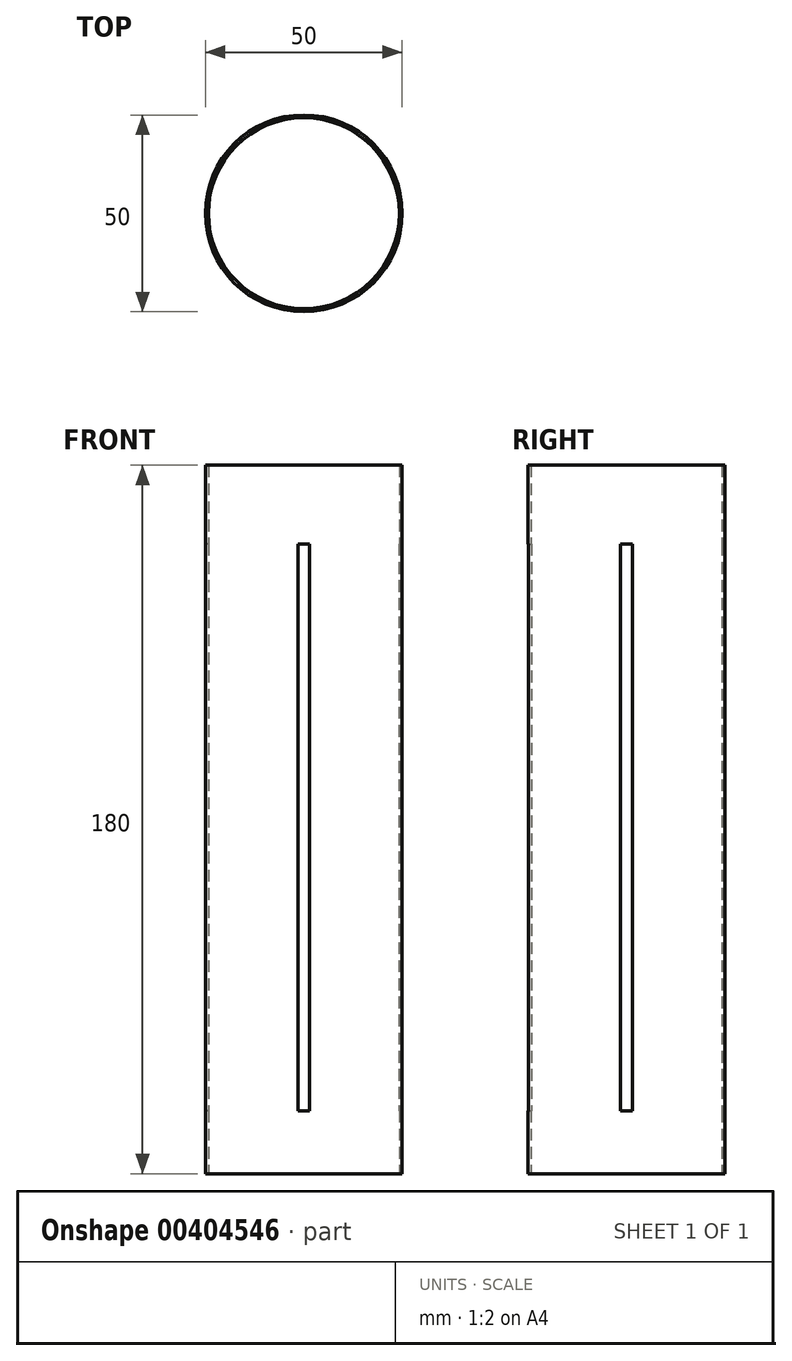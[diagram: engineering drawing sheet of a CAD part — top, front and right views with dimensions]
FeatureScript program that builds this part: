
annotation { "Feature Type Name" : "Feature", "Feature Type Description" : "" }
export const myFeature = defineFeature(function(context is Context, id is Id, definition is map)
    precondition{}
    {
        {
            var Q0;
            Q0=qCreatedBy(makeId("Top.planeOp"),FACE);
            var sketch = newSketch(context, id + "F0", { "sketchPlane" : qUnion([Q0])});
            skCircle(sketch, "E0", {"center": v(0, 0) * mm, "radius": 24.25 * mm});
            skCircle(sketch, "E1", {"center": v(0, 0) * mm, "radius": 25 * mm});
            skCircle(sketch, "E2", {"center": v(0, 0) * mm, "radius": 23.25 * mm});
            skSolve(sketch);
        }
        {
            var Q0;
            Q0=makeQuery(id+"F0.imprint","IMPRINT",FACE,{"disambiguationData":[TD([[makeQuery(id+"F0.imprint","IMPRINT",EDGE,{"derivedFrom":sQuery(id+"F0.wireOp",EDGE,"E0")}),-1.0]])]});
            var Q1;
            Q1 = qSketchRegion(id + "F2", true);
            extrude(context, id + "F1", {"entities" : qUnion([Q0, Q1]), "depth" : 180 * mm});
        }
        {
            var Q0;
            Q0=qCreatedBy(makeId("Right.planeOp"),FACE);
            var sketch = newSketch(context, id + "F2", { "sketchPlane" : qUnion([Q0])});
            skPoint(sketch, "E3", {"position": v(-24.8, 0) * mm});
            skPoint(sketch, "E4", {"position": v(-24.94, 16) * mm});
            skPoint(sketch, "E5", {"position": v(-24.94, 160) * mm});
            skPoint(sketch, "E6", {"position": v(24.93, 0) * mm});
            skPoint(sketch, "E7", {"position": v(24.93, 16) * mm});
            skPoint(sketch, "E8", {"position": v(24.93, 160) * mm});
            skLineSegment(sketch, "E9", {"start": v(-24.8, 0) * mm, "end": v(-24.94, 16) * mm});
            skLineSegment(sketch, "E10", {"start": v(-24.94, 16) * mm, "end": v(-24.94, 160) * mm});
            skLineSegment(sketch, "E11", {"start": v(24.93, 0) * mm, "end": v(24.93, 16) * mm});
            skLineSegment(sketch, "E12", {"start": v(24.93, 16) * mm, "end": v(24.93, 160) * mm});
            skPoint(sketch, "E13", {"position": v(-31.51, 160) * mm});
            skPoint(sketch, "E14", {"position": v(-31.6, 16) * mm});
            skPoint(sketch, "E15", {"position": v(-31.51, 0) * mm});
            skLineSegment(sketch, "E16", {"start": v(-31.51, 160) * mm, "end": v(-31.51, 0) * mm});
            skLineSegment(sketch, "E17", {"start": v(-31.51, 160) * mm, "end": v(-24.94, 160) * mm});
            skLineSegment(sketch, "E18", {"start": v(-31.51, 0) * mm, "end": v(-24.8, 0) * mm});
            skLineSegment(sketch, "E19", {"start": v(-31.6, 16) * mm, "end": v(-24.94, 16) * mm});
            skLineSegment(sketch, "E20", {"start": v(-56.53, 16) * mm, "end": v(47.01, 16) * mm});
            skLineSegment(sketch, "E21", {"start": v(-56.08, 0) * mm, "end": v(53.13, 0) * mm});
            skPoint(sketch, "E22", {"position": v(32.4, 160) * mm});
            skPoint(sketch, "E23", {"position": v(32.4, 16) * mm});
            skPoint(sketch, "E24", {"position": v(32.4, 0) * mm});
            skLineSegment(sketch, "E25", {"start": v(32.4, 160) * mm, "end": v(32.4, 16) * mm});
            skLineSegment(sketch, "E26", {"start": v(32.4, 0) * mm, "end": v(32.4, 16) * mm});
            skLineSegment(sketch, "E27", {"start": v(32.4, 160) * mm, "end": v(24.93, 160) * mm});
            skSolve(sketch);
        }
        {
            var Q0;
            {var subQ0=sQuery(id+"F2.wireOp",EDGE,"E10");Q0=makeQuery(id+"F2.imprint","IMPRINT",FACE,{"disambiguationData":[TD([[makeQuery(id+"F2.imprint","IMPRINT",EDGE,{"derivedFrom":subQ0}),1.0]])]});}
            var Q1;
            {var subQ0=sQuery(id+"F2.wireOp",EDGE,"E12");Q1=makeQuery(id+"F2.imprint","IMPRINT",FACE,{"disambiguationData":[TD([[makeQuery(id+"F2.imprint","IMPRINT",EDGE,{"derivedFrom":subQ0}),-1.0]])]});}
            extrude(context, id + "F3", {"entities" : qUnion([Q0, Q1]), "operationType" : NewBodyOperationType.REMOVE, "endBound" : BoundingType.SYMMETRIC, "depth" : 3 * mm});
        }
        {
            var Q0;
            Q0=makeQuery(id+"F3.boolean.opBoolean","COPY",FACE,{"derivedFrom":makeQuery(id+"F3.opExtrude","SWEPT_FACE",FACE,{"disambiguationData":[OSD([sQuery(id+"F2.wireOp",EDGE,"E10")])]})});
            var Q1;
            Q1=makeQuery(id+"F3.boolean.opBoolean","COPY",FACE,{"derivedFrom":makeQuery(id+"F3.opExtrude","SWEPT_FACE",FACE,{"disambiguationData":[OSD([sQuery(id+"F2.wireOp",EDGE,"E12")])]})});
            extrude(context, id + "F4", {"entities" : qUnion([Q0, Q1]), "operationType" : NewBodyOperationType.REMOVE, "oppositeDirection" : true, "depth" : 4 * mm});
        }
        {
            var Q0;
            Q0=makeQuery(id+"F3.boolean.opBoolean","COPY",FACE,{"derivedFrom":makeQuery(id+"F3.opExtrude","SWEPT_FACE",FACE,{"disambiguationData":[OSD([sQuery(id+"F2.wireOp",EDGE,"E12")])]})});
            extrude(context, id + "F5", {"entities" : qUnion([Q0]), "operationType" : NewBodyOperationType.REMOVE, "oppositeDirection" : true, "depth" : 4 * mm});
        }
        {
            var Q0;
            Q0=qCreatedBy(makeId("Front.planeOp"),FACE);
            var sketch = newSketch(context, id + "F6", { "sketchPlane" : qUnion([Q0])});
            skPoint(sketch, "E28", {"position": v(-24.85, 0) * mm});
            skPoint(sketch, "E29", {"position": v(-24.7, 16) * mm});
            skPoint(sketch, "E30", {"position": v(-24.7, 160) * mm});
            skPoint(sketch, "E31", {"position": v(24.76, 0) * mm});
            skPoint(sketch, "E32", {"position": v(24.76, 16) * mm});
            skPoint(sketch, "E33", {"position": v(24.76, 160) * mm});
            skLineSegment(sketch, "E34", {"start": v(-24.85, 0) * mm, "end": v(-24.7, 16) * mm});
            skLineSegment(sketch, "E35", {"start": v(-24.7, 16) * mm, "end": v(-24.7, 160) * mm});
            skLineSegment(sketch, "E36", {"start": v(24.76, 0) * mm, "end": v(24.76, 16) * mm});
            skLineSegment(sketch, "E37", {"start": v(24.76, 16) * mm, "end": v(24.76, 160) * mm});
            skPoint(sketch, "E38", {"position": v(-31.87, 160) * mm});
            skPoint(sketch, "E39", {"position": v(-31.96, 16) * mm});
            skPoint(sketch, "E40", {"position": v(-31.87, 0) * mm});
            skLineSegment(sketch, "E41", {"start": v(-31.87, 160) * mm, "end": v(-31.87, 0) * mm});
            skLineSegment(sketch, "E42", {"start": v(-31.87, 160) * mm, "end": v(-24.7, 160) * mm});
            skLineSegment(sketch, "E43", {"start": v(-56.89, 16) * mm, "end": v(46.66, 16) * mm});
            skLineSegment(sketch, "E44", {"start": v(-56.43, 0) * mm, "end": v(52.78, 0) * mm});
            skPoint(sketch, "E45", {"position": v(32.05, 160) * mm});
            skPoint(sketch, "E46", {"position": v(32.05, 16) * mm});
            skPoint(sketch, "E47", {"position": v(32.05, 0) * mm});
            skLineSegment(sketch, "E48", {"start": v(32.05, 160) * mm, "end": v(32.05, 16) * mm});
            skLineSegment(sketch, "E49", {"start": v(32.05, 160) * mm, "end": v(24.76, 160) * mm});
            skLineSegment(sketch, "E50", {"start": v(32.05, 0) * mm, "end": v(32.05, 16) * mm});
            skSolve(sketch);
        }
        {
            var Q0;
            {var subQ0=sQuery(id+"F6.wireOp",EDGE,"E37");Q0=makeQuery(id+"F6.imprint","IMPRINT",FACE,{"disambiguationData":[TD([[makeQuery(id+"F6.imprint","IMPRINT",EDGE,{"derivedFrom":subQ0}),-1.0]])]});}
            var Q1;
            {var subQ0=sQuery(id+"F6.wireOp",EDGE,"E35");Q1=makeQuery(id+"F6.imprint","IMPRINT",FACE,{"disambiguationData":[TD([[makeQuery(id+"F6.imprint","IMPRINT",EDGE,{"derivedFrom":subQ0}),1.0]])]});}
            extrude(context, id + "F7", {"entities" : qUnion([Q0, Q1]), "operationType" : NewBodyOperationType.ADD, "endBound" : BoundingType.SYMMETRIC, "depth" : 3 * mm});
        }
        {
            var Q0;
            Q0=makeQuery(id+"F7.opExtrude","SWEPT_FACE",FACE,{"disambiguationData":[OSD([sQuery(id+"F6.wireOp",EDGE,"E48")])]});
            var Q1;
            Q1=makeQuery(id+"F7.opExtrude","SWEPT_FACE",FACE,{"disambiguationData":[OSD([sQuery(id+"F6.wireOp",EDGE,"E41")])]});
            extrude(context, id + "F8", {"entities" : qUnion([Q0, Q1]), "operationType" : NewBodyOperationType.REMOVE, "oppositeDirection" : true, "depth" : 4 * mm});
        }
        {
            var Q0;
            Q0=makeQuery(id+"F8.boolean.opBoolean","COPY",FACE,{"derivedFrom":makeQuery(id+"F8.opExtrude","CAP_FACE",FACE,{"disambiguationData":[OSD([sQuery(id+"F6.wireOp",EDGE,"E48")])],"isStart":false})});
            extrude(context, id + "F9", {"entities" : qUnion([Q0]), "operationType" : NewBodyOperationType.REMOVE, "oppositeDirection" : true, "depth" : 25 * mm});
        }
        {
            var Q0;
            Q0=makeQuery(id+"F7.opExtrude","SWEPT_FACE",FACE,{"disambiguationData":[OSD([sQuery(id+"F6.wireOp",EDGE,"E41")])]});
            extrude(context, id + "F10", {"entities" : qUnion([Q0]), "operationType" : NewBodyOperationType.REMOVE, "oppositeDirection" : true, "depth" : 10 * mm});
        }
    });
